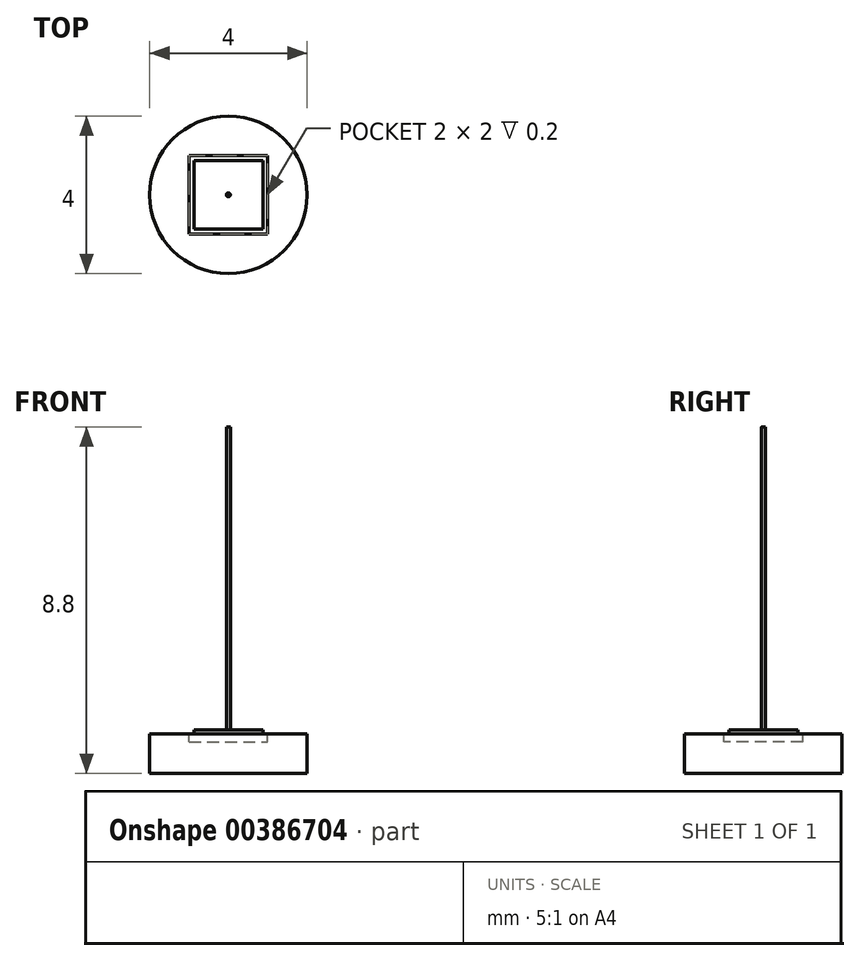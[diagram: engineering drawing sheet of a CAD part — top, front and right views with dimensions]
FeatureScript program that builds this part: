
annotation { "Feature Type Name" : "Feature", "Feature Type Description" : "" }
export const myFeature = defineFeature(function(context is Context, id is Id, definition is map)
    precondition{}
    {
        {
            var Q0;
            Q0=qCreatedBy(makeId("Top.planeOp"),FACE);
            var sketch = newSketch(context, id + "F0", { "sketchPlane" : qUnion([Q0])});
            skLineSegment(sketch, "E0.bottom", {"start": v(-0.87, 0.88) * mm, "end": v(0.88, 0.88) * mm});
            skLineSegment(sketch, "E0.top", {"start": v(-0.88, -0.88) * mm, "end": v(0.87, -0.88) * mm});
            skLineSegment(sketch, "E0.left", {"start": v(-0.87, 0.88) * mm, "end": v(-0.88, -0.87) * mm});
            skLineSegment(sketch, "E0.right", {"start": v(0.88, 0.88) * mm, "end": v(0.87, -0.87) * mm});
            skPoint(sketch, "E0.middle", {"position": v(0, 0) * mm});
            skSolve(sketch);
        }
        {
            var Q0;
            Q0=qCreatedBy(makeId("Top.planeOp"),FACE);
            cPlane(context, id + "F1", {"entities" : qUnion([Q0]), "cplaneType" : CPlaneType.OFFSET, "offset" : 7.8 * mm, "width" : 150 * mm, "height" : 150 * mm});
        }
        {
            var Q0;
            Q0=qCreatedBy(id+"F1.planeOp",FACE);
            var sketch = newSketch(context, id + "F2", { "sketchPlane" : qUnion([Q0])});
            skCircle(sketch, "E1", {"center": v(0, 0) * mm, "radius": 0.05 * mm});
            skSolve(sketch);
        }
        {
            var Q0;
            Q0=makeQuery(id+"F2.imprint","IMPRINT",FACE,{"disambiguationData":[TD([[makeQuery(id+"F2.imprint","IMPRINT",EDGE,{"derivedFrom":sQuery(id+"F2.wireOp",EDGE,"E1")}),1.0]])]});
            extrude(context, id + "F3", {"entities" : qUnion([Q0]), "oppositeDirection" : true, "depth" : 7.8 * mm});
        }
        {
            var Q0;
            Q0=makeQuery(id+"F0.imprint","IMPRINT",FACE,{"disambiguationData":[TD([[makeQuery(id+"F0.imprint","IMPRINT",EDGE,{"derivedFrom":sQuery(id+"F0.wireOp",EDGE,"E0.bottom")}),-1.0]])]});
            extrude(context, id + "F4", {"entities" : qUnion([Q0]), "operationType" : NewBodyOperationType.ADD, "depth" : .1 * mm});
        }
        {
            var Q0;
            Q0=qCreatedBy(makeId("Top.planeOp"),FACE);
            var sketch = newSketch(context, id + "F5", { "sketchPlane" : qUnion([Q0])});
            skCircle(sketch, "E2", {"center": v(0, 0) * mm, "radius": 2 * mm});
            skSolve(sketch);
        }
        {
            var Q0;
            Q0=makeQuery(id+"F5.imprint","IMPRINT",FACE,{"disambiguationData":[TD([[makeQuery(id+"F5.imprint","IMPRINT",EDGE,{"derivedFrom":sQuery(id+"F5.wireOp",EDGE,"E2")}),1.0]])]});
            extrude(context, id + "F6", {"entities" : qUnion([Q0]), "oppositeDirection" : true, "depth" : 1 * mm});
        }
        {
            var Q0;
            Q0=makeQuery(id+"F6.opExtrude","CAP_FACE",FACE,{"disambiguationData":[OSD([sQuery(id+"F5.wireOp",EDGE,"E2")])],"isStart":true});
            var sketch = newSketch(context, id + "F7", { "sketchPlane" : qUnion([Q0])});
            skLineSegment(sketch, "E3.bottom", {"start": v(-1, 1) * mm, "end": v(1, 1) * mm});
            skLineSegment(sketch, "E3.top", {"start": v(-1, -1) * mm, "end": v(1, -1) * mm});
            skLineSegment(sketch, "E3.left", {"start": v(-1, 1) * mm, "end": v(-1, -1) * mm});
            skLineSegment(sketch, "E3.right", {"start": v(1, 1) * mm, "end": v(1, -1) * mm});
            skPoint(sketch, "E3.middle", {"position": v(0, 0) * mm});
            skSolve(sketch);
        }
        {
            var Q0;
            Q0=makeQuery(id+"F7.imprint","IMPRINT",FACE,{"disambiguationData":[TD([[makeQuery(id+"F7.imprint","IMPRINT",EDGE,{"derivedFrom":sQuery(id+"F7.wireOp",EDGE,"E3.bottom")}),-1.0]])]});
            extrude(context, id + "F8", {"entities" : qUnion([Q0]), "operationType" : NewBodyOperationType.REMOVE, "oppositeDirection" : true, "depth" : .2 * mm});
        }
    });
